# Revit family: 1501a_lightowl_dt
name_source: partatom
category: Communication Devices
units: mm (PartAtom-declared; Revit-internal decimal feet)

## family parameters
Cut with Voids When Loaded = No
Host = Face
Maintain Annotation Orientation = No
OmniClass Number = 23.85.80.11.27
OmniClass Title = Lighting Controls
Part Type = Normal
Room Calculation Point = No
Round Connector Dimension = Use Diameter
Shared = Yes

## types (1)
- 1501a_lightowl_dt
    Assembly Code = D5090
    Certifications = UL and cUL listed
    Default Elevation = 48 "
    Description = The LightOWL Dual Technology Ultrasonic and Passive Infrared Sensor combines
ultrasonic (US) and passive infrared (PIR) technologies to turn lighting on and off
based on occupancy. Designed specifically for areas where ceiling sensors are not
appropriate, this sensor features Controls' patented IntelliDAPT® technology,
which makes all the sensor adjustments automatically
    Feartures = IntelliDAPT self-adaptive technology—no manual adjustment required
All-digital dual technology passive infrared (PIR) and ultrasonic (US) sensor 
Non-volatile memory for sensor settings
1,600 square-foot coverage area 
Optional relay and photocell control 
Optional Quick-to-Install (QTI) connector 
UL and cUL listed 
California Title 24 compliant 
Five-year limited warranty 
Low voltage device: 24 Vdc
    Housing Material = Paint - Matte White
    Manufacturer = NX Lighting Controls
    Model = NX Ceiling Mount Occupancy Sensors employ Passive Infrared
and Ultrasonic sensing technologies to turn lighting on and off based
on occupancy
    Power Requirements = 24VDC, 33 mA (uses UVPP and MP-Series power pack—not included)
    Sensing Element = Metal-Nickel
    Type Comments = Wall Mount Occupancy Sensors
    URL = https://www.currentlighting.com
    Warranty = 5-Years Warranty

## geometry (parser evidence)
native form markers: Sweep x4
no freeform markers — native parametric forms only
